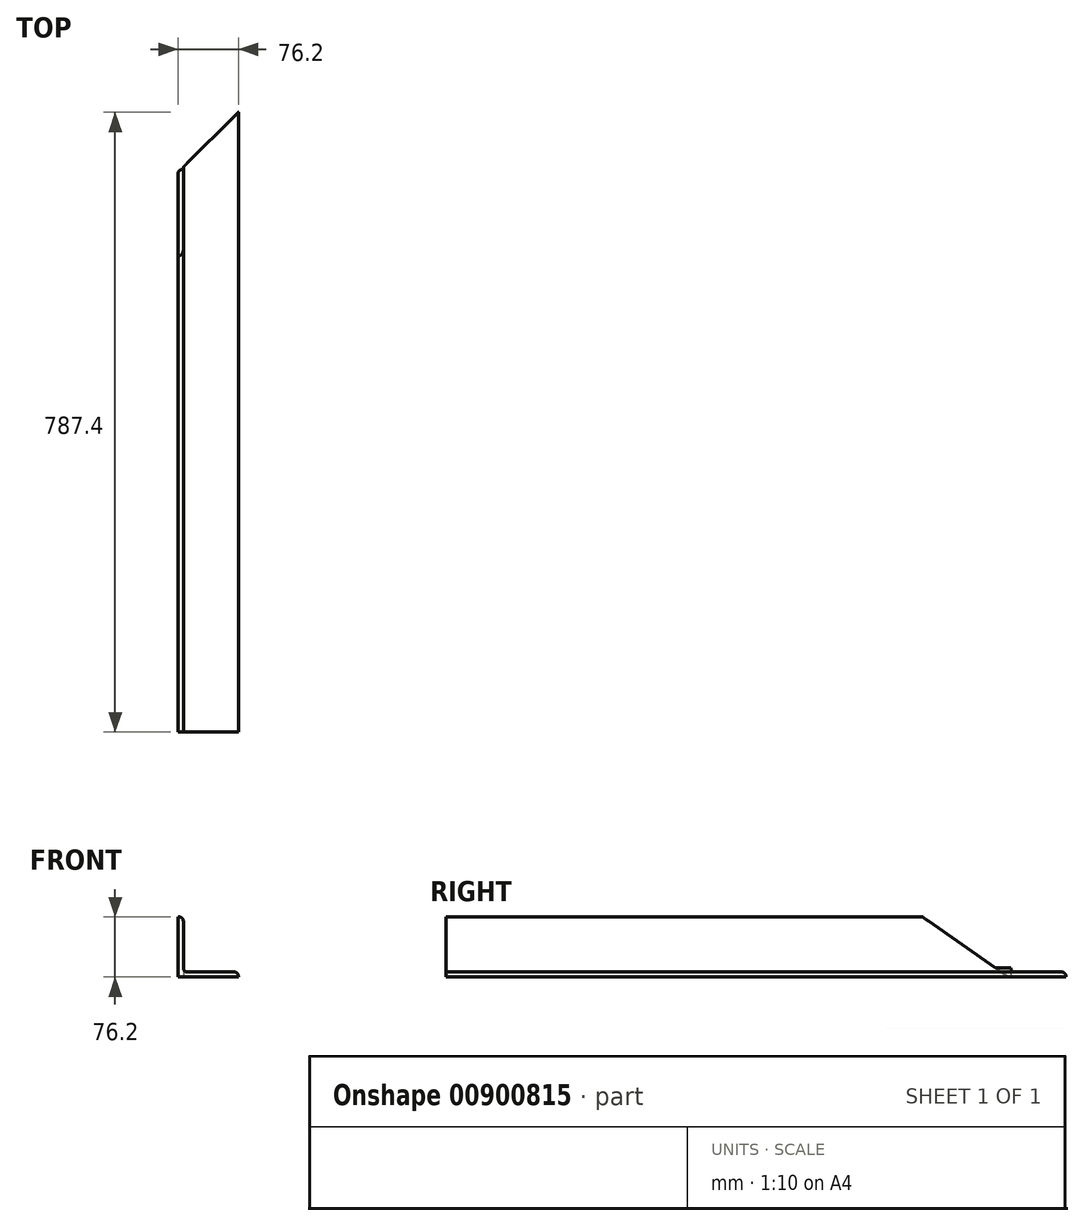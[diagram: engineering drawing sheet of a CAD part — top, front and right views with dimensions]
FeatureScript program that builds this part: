
annotation { "Feature Type Name" : "Feature", "Feature Type Description" : "" }
export const myFeature = defineFeature(function(context is Context, id is Id, definition is map)
    precondition{}
    {
        {
            var Q0;
            Q0=qCreatedBy(makeId("Front.planeOp"),FACE);
            var sketch = newSketch(context, id + "F0", { "sketchPlane" : qUnion([Q0])});
            skLineSegment(sketch, "E0.bottom", {"start": v(38.1, -38.1) * mm, "end": v(-38.1, -38.1) * mm});
            skLineSegment(sketch, "E0.top", {"start": v(-31.75, 38.1) * mm, "end": v(-38.1, 38.1) * mm});
            skLineSegment(sketch, "E0.left", {"start": v(38.1, -38.1) * mm, "end": v(38.1, -31.75) * mm});
            skLineSegment(sketch, "E0.right", {"start": v(-38.1, -38.1) * mm, "end": v(-38.1, 38.1) * mm});
            skPoint(sketch, "E0.middle", {"position": v(0, 0) * mm});
            skLineSegment(sketch, "E1.0", {"start": v(-31.75, -31.75) * mm, "end": v(-31.75, 38.1) * mm});
            skLineSegment(sketch, "E2.0", {"start": v(38.1, -31.75) * mm, "end": v(-31.75, -31.75) * mm});
            skPoint(sketch, "E3.orphan", {"position": v(38.1, 38.1) * mm});
            skSolve(sketch);
        }
        {
            var Q0;
            Q0 = qSketchRegion(id + "F0", true);
            extrude(context, id + "F1", {"entities" : qUnion([Q0]), "depth" : 787.4 * mm, "offsetDistance" : 25.4 * mm, "symmetric" : true});
        }
        {
            var Q0;
            Q0=makeQuery(id+"F1.opExtrude","SWEPT_EDGE",EDGE,{"disambiguationData":[OSD([sQuery(id+"F0.wireOp",EDGE,"E0.top"),sQuery(id+"F0.wireOp",EDGE,"E1.0")])]});
            var Q1;
            Q1=makeQuery(id+"F1.opExtrude","SWEPT_EDGE",EDGE,{"disambiguationData":[OSD([sQuery(id+"F0.wireOp",EDGE,"E1.0"),sQuery(id+"F0.wireOp",EDGE,"E2.0")])]});
            var Q2;
            Q2=makeQuery(id+"F1.opExtrude","SWEPT_EDGE",EDGE,{"disambiguationData":[OSD([sQuery(id+"F0.wireOp",EDGE,"E0.left"),sQuery(id+"F0.wireOp",EDGE,"E2.0")])]});
            fillet(context, id + "F2", {"entities" : qUnion([Q0, Q1, Q2]), "radius" : 5.08 * mm, "tangentPropagation" : true, "allowEdgeOverflow" : false});
        }
        {
            var Q0;
            Q0=makeQuery(id+"F1.opExtrude","SWEPT_FACE",FACE,{"disambiguationData":[OSD([sQuery(id+"F0.wireOp",EDGE,"E0.bottom")])]});
            var sketch = newSketch(context, id + "F3", { "sketchPlane" : qUnion([Q0])});
            skLineSegment(sketch, "E4", {"start": v(38.1, -393.7) * mm, "end": v(-38.1, -317.5) * mm});
            skLineSegment(sketch, "E5", {"start": v(-38.1, -317.5) * mm, "end": v(-38.1, -393.7) * mm});
            skLineSegment(sketch, "E6", {"start": v(-38.1, -393.7) * mm, "end": v(38.1, -393.7) * mm});
            skSolve(sketch);
        }
        {
            var Q0;
            Q0 = qSketchRegion(id + "F3", true);
            extrude(context, id + "F4", {"entities" : qUnion([Q0]), "operationType" : NewBodyOperationType.REMOVE, "oppositeDirection" : true, "depth" : 76.2 * mm, "offsetDistance" : 25.4 * mm});
        }
        {
            var Q0;
            Q0=makeQuery(id+"F1.opExtrude","SWEPT_FACE",FACE,{"disambiguationData":[OSD([sQuery(id+"F0.wireOp",EDGE,"E1.0")])]});
            var sketch = newSketch(context, id + "F5", { "sketchPlane" : qUnion([Q0])});
            skLineSegment(sketch, "E7", {"start": v(323.85, -40.38) * mm, "end": v(200.33, 46.1) * mm});
            skLineSegment(sketch, "E8", {"start": v(200.33, 46.1) * mm, "end": v(323.85, 46.1) * mm});
            skLineSegment(sketch, "E9", {"start": v(323.85, 46.1) * mm, "end": v(323.85, -40.38) * mm});
            skSolve(sketch);
        }
        {
            var Q0;
            Q0 = qSketchRegion(id + "F5", true);
            extrude(context, id + "F6", {"entities" : qUnion([Q0]), "operationType" : NewBodyOperationType.REMOVE, "oppositeDirection" : true, "depth" : 25.4 * mm, "offsetDistance" : 25.4 * mm});
        }
    });
